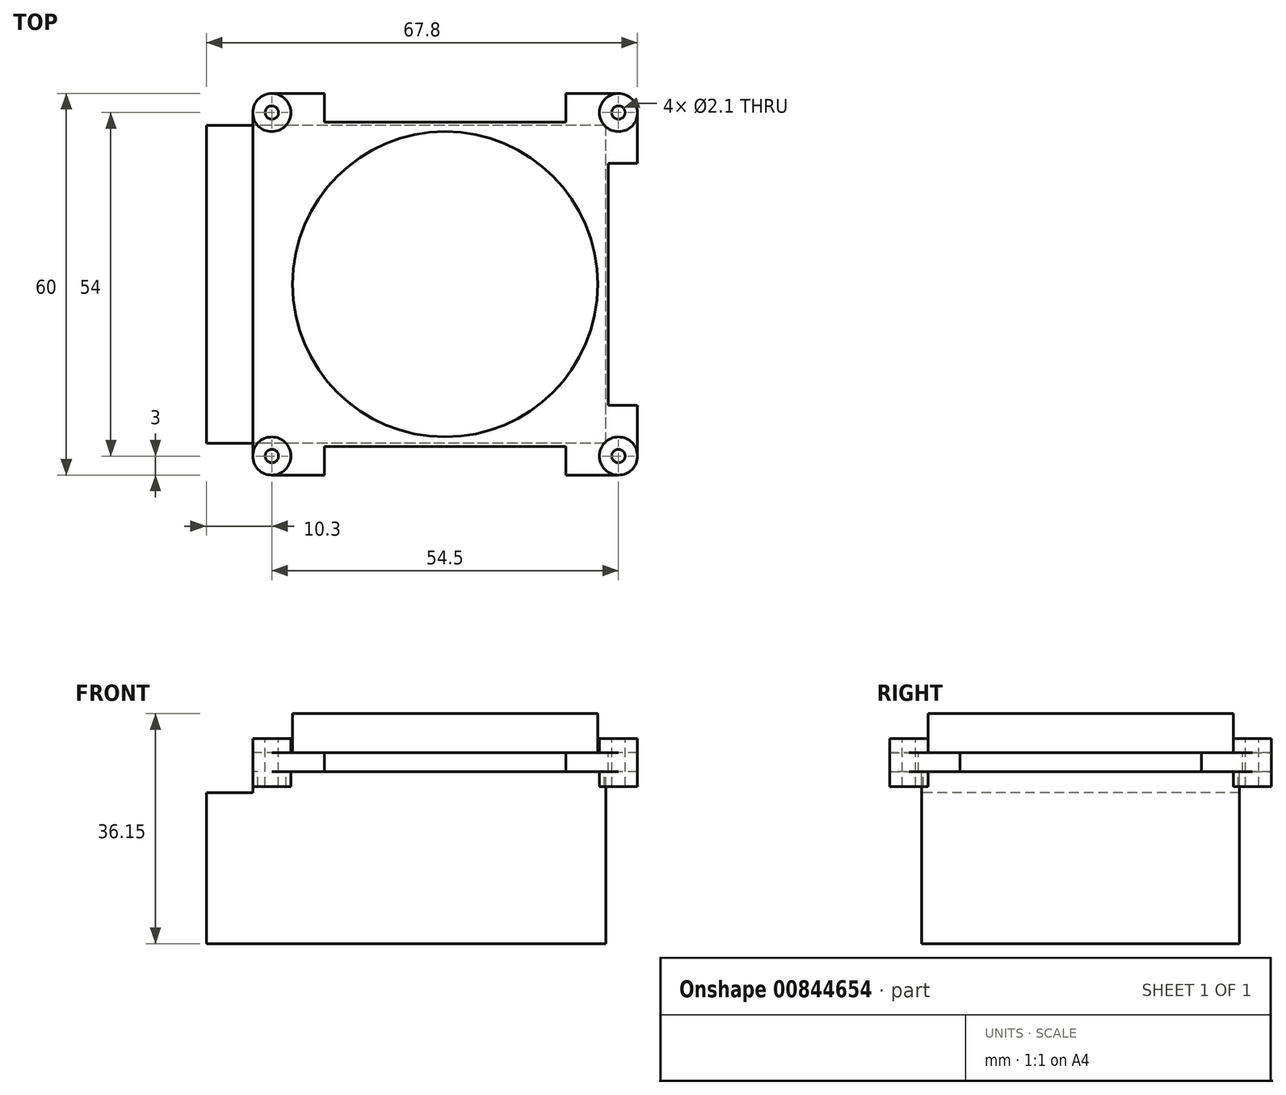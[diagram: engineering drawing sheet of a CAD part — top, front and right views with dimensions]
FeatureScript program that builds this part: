
annotation { "Feature Type Name" : "Feature", "Feature Type Description" : "" }
export const myFeature = defineFeature(function(context is Context, id is Id, definition is map)
    precondition{}
    {
        {
            var Q0;
            Q0=qCreatedBy(makeId("Top.planeOp"),FACE);
            var sketch = newSketch(context, id + "F0", { "sketchPlane" : qUnion([Q0])});
            skLineSegment(sketch, "E0.bottom", {"start": v(27.25, 30) * mm, "end": v(19, 30) * mm});
            skLineSegment(sketch, "E0.top", {"start": v(27.25, -30) * mm, "end": v(19, -30) * mm});
            skLineSegment(sketch, "E0.left", {"start": v(30.25, 27) * mm, "end": v(30.25, -27) * mm});
            skLineSegment(sketch, "E0.right", {"start": v(-30.25, 27) * mm, "end": v(-30.25, -27) * mm});
            skPoint(sketch, "E0.middle", {"position": v(0, 0) * mm});
            skCircle(sketch, "E1", {"center": v(0, 0) * mm, "radius": 24 * mm});
            skCircle(sketch, "E2", {"center": v(27.25, 27) * mm, "radius": 3 * mm});
            skCircle(sketch, "E3", {"center": v(-27.25, 27) * mm, "radius": 3 * mm});
            skCircle(sketch, "E4", {"center": v(-27.25, -27) * mm, "radius": 3 * mm});
            skCircle(sketch, "E5", {"center": v(27.25, -27) * mm, "radius": 3 * mm});
            skPoint(sketch, "E6.orphan", {"position": v(-30.25, 30) * mm});
            skPoint(sketch, "E7.orphan", {"position": v(30.25, 30) * mm});
            skPoint(sketch, "E8.orphan", {"position": v(30.25, -30) * mm});
            skPoint(sketch, "E9.orphan", {"position": v(-30.25, -30) * mm});
            skCircle(sketch, "E10", {"center": v(-27.25, 27) * mm, "radius": 1.05 * mm});
            skCircle(sketch, "E11", {"center": v(-27.25, -27) * mm, "radius": 1.05 * mm});
            skCircle(sketch, "E12", {"center": v(27.25, -27) * mm, "radius": 1.05 * mm});
            skCircle(sketch, "E13", {"center": v(27.25, 27) * mm, "radius": 1.05 * mm});
            skLineSegment(sketch, "E14.top", {"start": v(-19, 25.5) * mm, "end": v(19, 25.5) * mm});
            skLineSegment(sketch, "E14.left", {"start": v(-19, 30) * mm, "end": v(-19, 25.5) * mm});
            skLineSegment(sketch, "E14.right", {"start": v(19, 30) * mm, "end": v(19, 25.5) * mm});
            skLineSegment(sketch, "E15.trimOffspring", {"start": v(-19, 30) * mm, "end": v(-27.25, 30) * mm});
            skLineSegment(sketch, "E16.MirrorCS", {"start": v(-19, -30) * mm, "end": v(-19, -25.5) * mm});
            skLineSegment(sketch, "E17.MirrorCS", {"start": v(-19, -25.5) * mm, "end": v(19, -25.5) * mm});
            skLineSegment(sketch, "E18.MirrorCS", {"start": v(19, -30) * mm, "end": v(19, -25.5) * mm});
            skLineSegment(sketch, "E19.trimOffspring", {"start": v(-19, -30) * mm, "end": v(-27.25, -30) * mm});
            skLineSegment(sketch, "E20.bottom", {"start": v(30.25, -19) * mm, "end": v(25.65, -19) * mm});
            skLineSegment(sketch, "E20.top", {"start": v(30.25, 19) * mm, "end": v(25.65, 19) * mm});
            skLineSegment(sketch, "E20.left", {"start": v(30.25, -19) * mm, "end": v(30.25, 19) * mm});
            skLineSegment(sketch, "E20.right", {"start": v(25.65, -19) * mm, "end": v(25.65, 19) * mm});
            skSolve(sketch);
        }
        {
            var Q0;
            Q0=makeQuery(id+"F0.imprint","IMPRINT",FACE,{"disambiguationData":[TD([[makeQuery(id+"F0.imprint","IMPRINT",EDGE,{"derivedFrom":sQuery(id+"F0.wireOp",EDGE,"E1")}),1.0]])]});
            extrude(context, id + "F1", {"entities" : qUnion([Q0]), "depth" : 6.15 * mm, "offsetDistance" : 25 * mm});
        }
        {
            var Q0;
            Q0=makeQuery(id+"F0.imprint","IMPRINT",FACE,{"disambiguationData":[TD([[makeQuery(id+"F0.imprint","IMPRINT",EDGE,{"derivedFrom":sQuery(id+"F0.wireOp",EDGE,"E12")}),-1.0]])]});
            var Q1;
            Q1=makeQuery(id+"F0.imprint","IMPRINT",FACE,{"disambiguationData":[TD([[makeQuery(id+"F0.imprint","IMPRINT",EDGE,{"derivedFrom":sQuery(id+"F0.wireOp",EDGE,"E13")}),-1.0]])]});
            var Q2;
            Q2=makeQuery(id+"F0.imprint","IMPRINT",FACE,{"disambiguationData":[TD([[makeQuery(id+"F0.imprint","IMPRINT",EDGE,{"derivedFrom":sQuery(id+"F0.wireOp",EDGE,"E10")}),-1.0]])]});
            var Q3;
            Q3=makeQuery(id+"F0.imprint","IMPRINT",FACE,{"disambiguationData":[TD([[makeQuery(id+"F0.imprint","IMPRINT",EDGE,{"derivedFrom":sQuery(id+"F0.wireOp",EDGE,"E11")}),-1.0]])]});
            extrude(context, id + "F2", {"entities" : qUnion([Q0, Q1, Q2, Q3]), "depth" : 2.25 * mm, "offsetDistance" : 25 * mm});
        }
        {
            var Q0;
            Q0=makeQuery(id+"F0.imprint","IMPRINT",FACE,{"disambiguationData":[TD([[makeQuery(id+"F0.imprint","IMPRINT",EDGE,{"derivedFrom":sQuery(id+"F0.wireOp",EDGE,"E11")}),-1.0]])]});
            var Q1;
            Q1=makeQuery(id+"F0.imprint","IMPRINT",FACE,{"disambiguationData":[TD([[makeQuery(id+"F0.imprint","IMPRINT",EDGE,{"derivedFrom":sQuery(id+"F0.wireOp",EDGE,"E10")}),-1.0]])]});
            var Q2;
            Q2=makeQuery(id+"F0.imprint","IMPRINT",FACE,{"disambiguationData":[TD([[makeQuery(id+"F0.imprint","IMPRINT",EDGE,{"derivedFrom":sQuery(id+"F0.wireOp",EDGE,"E12")}),-1.0]])]});
            var Q3;
            Q3=makeQuery(id+"F0.imprint","IMPRINT",FACE,{"disambiguationData":[TD([[makeQuery(id+"F0.imprint","IMPRINT",EDGE,{"derivedFrom":sQuery(id+"F0.wireOp",EDGE,"E13")}),-1.0]])]});
            extrude(context, id + "F3", {"entities" : qUnion([Q0, Q1, Q2, Q3]), "oppositeDirection" : true, "depth" : 5.3 * mm, "offsetDistance" : 25 * mm});
        }
        {
            var Q0;
            {var subQ6=sQuery(id+"F0.wireOp",EDGE,"E0.bottom");Q0=makeQuery(id+"F0.imprint","IMPRINT",FACE,{"disambiguationData":[TD([[makeQuery(id+"F0.imprint","IMPRINT",EDGE,{"derivedFrom":subQ6}),1.0]])]});}
            extrude(context, id + "F4", {"entities" : qUnion([Q0]), "oppositeDirection" : true, "depth" : 3 * mm, "offsetDistance" : 25 * mm});
        }
        {
            var Q0;
            Q0=makeQuery(id+"F4.opExtrude","SWEPT_BODY",BODY,{"disambiguationData":[OSD([sQuery(id+"F0.wireOp",EDGE,"E0.bottom"),sQuery(id+"F0.wireOp",EDGE,"E0.top"),sQuery(id+"F0.wireOp",EDGE,"E0.left"),sQuery(id+"F0.wireOp",EDGE,"E0.right"),sQuery(id+"F0.wireOp",EDGE,"E1"),sQuery(id+"F0.wireOp",EDGE,"E2"),sQuery(id+"F0.wireOp",EDGE,"E3"),sQuery(id+"F0.wireOp",EDGE,"E4"),sQuery(id+"F0.wireOp",EDGE,"E5"),sQuery(id+"F0.wireOp",EDGE,"E14.top"),sQuery(id+"F0.wireOp",EDGE,"E14.left"),sQuery(id+"F0.wireOp",EDGE,"E14.right"),sQuery(id+"F0.wireOp",EDGE,"E15.trimOffspring"),sQuery(id+"F0.wireOp",EDGE,"E16.MirrorCS"),sQuery(id+"F0.wireOp",EDGE,"E17.MirrorCS"),sQuery(id+"F0.wireOp",EDGE,"E18.MirrorCS"),sQuery(id+"F0.wireOp",EDGE,"E19.trimOffspring")])]});
            var Q1;
            Q1=makeQuery(id+"F3.opExtrude","SWEPT_BODY",BODY,{"disambiguationData":[OSD([sQuery(id+"F0.wireOp",EDGE,"E5"),sQuery(id+"F0.wireOp",EDGE,"E12")])]});
            var Q2;
            Q2=makeQuery(id+"F3.opExtrude","SWEPT_BODY",BODY,{"disambiguationData":[OSD([sQuery(id+"F0.wireOp",EDGE,"E4"),sQuery(id+"F0.wireOp",EDGE,"E11")])]});
            var Q3;
            Q3=makeQuery(id+"F3.opExtrude","SWEPT_BODY",BODY,{"disambiguationData":[OSD([sQuery(id+"F0.wireOp",EDGE,"E3"),sQuery(id+"F0.wireOp",EDGE,"E10")])]});
            var Q4;
            Q4=makeQuery(id+"F3.opExtrude","SWEPT_BODY",BODY,{"disambiguationData":[OSD([sQuery(id+"F0.wireOp",EDGE,"E2"),sQuery(id+"F0.wireOp",EDGE,"E13")])]});
            var Q5;
            Q5=makeQuery(id+"F2.opExtrude","SWEPT_BODY",BODY,{"disambiguationData":[OSD([sQuery(id+"F0.wireOp",EDGE,"E5"),sQuery(id+"F0.wireOp",EDGE,"E12")])]});
            var Q6;
            Q6=makeQuery(id+"F2.opExtrude","SWEPT_BODY",BODY,{"disambiguationData":[OSD([sQuery(id+"F0.wireOp",EDGE,"E4"),sQuery(id+"F0.wireOp",EDGE,"E11")])]});
            var Q7;
            Q7=makeQuery(id+"F2.opExtrude","SWEPT_BODY",BODY,{"disambiguationData":[OSD([sQuery(id+"F0.wireOp",EDGE,"E3"),sQuery(id+"F0.wireOp",EDGE,"E10")])]});
            var Q8;
            Q8=makeQuery(id+"F2.opExtrude","SWEPT_BODY",BODY,{"disambiguationData":[OSD([sQuery(id+"F0.wireOp",EDGE,"E2"),sQuery(id+"F0.wireOp",EDGE,"E13")])]});
            var Q9;
            Q9=makeQuery(id+"F1.opExtrude","SWEPT_BODY",BODY,{"disambiguationData":[OSD([sQuery(id+"F0.wireOp",EDGE,"E1")])]});
            booleanBodies(context, id + "F5", {"operationType" : BooleanOperationType.UNION, "tools" : qUnion([Q0, Q1, Q2, Q3, Q4, Q5, Q6, Q7, Q8, Q9])});
        }
        {
            var Q0;
            Q0=makeQuery(id+"F0.imprint","IMPRINT",FACE,{"disambiguationData":[TD([[makeQuery(id+"F0.imprint","IMPRINT",EDGE,{"derivedFrom":sQuery(id+"F0.wireOp",EDGE,"E1")}),1.0]])]});
            var sketch = newSketch(context, id + "F6", { "sketchPlane" : qUnion([Q0])});
            skLineSegment(sketch, "E21.bottom", {"start": v(25.25, -25) * mm, "end": v(-30.25, -25) * mm});
            skLineSegment(sketch, "E21.top", {"start": v(25.25, 25) * mm, "end": v(-30.25, 25) * mm});
            skLineSegment(sketch, "E21.left", {"start": v(25.25, -25) * mm, "end": v(25.25, 25) * mm});
            skLineSegment(sketch, "E21.right", {"start": v(-30.25, -25) * mm, "end": v(-30.25, 25) * mm});
            skSolve(sketch);
        }
        {
            var Q0;
            Q0 = qSketchRegion(id + "F6", true);
            extrude(context, id + "F7", {"entities" : qUnion([Q0]), "oppositeDirection" : true, "depth" : 30 * mm, "offsetDistance" : 25 * mm});
        }
        {
            var Q0;
            Q0=makeQuery(id+"F4.opExtrude","SWEPT_BODY",BODY,{"disambiguationData":[OSD([sQuery(id+"F0.wireOp",EDGE,"E0.bottom"),sQuery(id+"F0.wireOp",EDGE,"E0.top"),sQuery(id+"F0.wireOp",EDGE,"E0.left"),sQuery(id+"F0.wireOp",EDGE,"E0.right"),sQuery(id+"F0.wireOp",EDGE,"E1"),sQuery(id+"F0.wireOp",EDGE,"E2"),sQuery(id+"F0.wireOp",EDGE,"E3"),sQuery(id+"F0.wireOp",EDGE,"E4"),sQuery(id+"F0.wireOp",EDGE,"E5"),sQuery(id+"F0.wireOp",EDGE,"E14.top"),sQuery(id+"F0.wireOp",EDGE,"E14.left"),sQuery(id+"F0.wireOp",EDGE,"E14.right"),sQuery(id+"F0.wireOp",EDGE,"E15.trimOffspring"),sQuery(id+"F0.wireOp",EDGE,"E16.MirrorCS"),sQuery(id+"F0.wireOp",EDGE,"E17.MirrorCS"),sQuery(id+"F0.wireOp",EDGE,"E18.MirrorCS"),sQuery(id+"F0.wireOp",EDGE,"E19.trimOffspring")])]});
            var Q1;
            {var subQ0=sQuery(id+"F0.wireOp",EDGE,"E5");var subQ1=sQuery(id+"F0.wireOp",EDGE,"E4");var subQ2=sQuery(id+"F0.wireOp",EDGE,"E3");var subQ3=sQuery(id+"F0.wireOp",EDGE,"E2");var subQ4=sQuery(id+"F0.wireOp",EDGE,"E1");var subQ5=sQuery(id+"F0.wireOp",EDGE,"E12");var subQ6=sQuery(id+"F0.wireOp",EDGE,"E11");var subQ7=sQuery(id+"F0.wireOp",EDGE,"E10");var subQ8=sQuery(id+"F0.wireOp",EDGE,"E13");Q1=makeQuery(id+"F5.opBoolean","MERGE",BODY,{"derivedFrom":[makeQuery(id+"F1.opExtrude","SWEPT_BODY",BODY,{"disambiguationData":[OSD([subQ4])]}),makeQuery(id+"F2.opExtrude","SWEPT_BODY",BODY,{"disambiguationData":[OSD([subQ3,subQ8])]}),makeQuery(id+"F2.opExtrude","SWEPT_BODY",BODY,{"disambiguationData":[OSD([subQ2,subQ7])]}),makeQuery(id+"F2.opExtrude","SWEPT_BODY",BODY,{"disambiguationData":[OSD([subQ1,subQ6])]}),makeQuery(id+"F2.opExtrude","SWEPT_BODY",BODY,{"disambiguationData":[OSD([subQ0,subQ5])]}),makeQuery(id+"F3.opExtrude","SWEPT_BODY",BODY,{"disambiguationData":[OSD([subQ3,subQ8])]}),makeQuery(id+"F3.opExtrude","SWEPT_BODY",BODY,{"disambiguationData":[OSD([subQ2,subQ7])]}),makeQuery(id+"F3.opExtrude","SWEPT_BODY",BODY,{"disambiguationData":[OSD([subQ1,subQ6])]}),makeQuery(id+"F3.opExtrude","SWEPT_BODY",BODY,{"disambiguationData":[OSD([subQ0,subQ5])]}),makeQuery(id+"F4.opExtrude","SWEPT_BODY",BODY,{"disambiguationData":[OSD([sQuery(id+"F0.wireOp",EDGE,"E0.bottom"),sQuery(id+"F0.wireOp",EDGE,"E0.top"),sQuery(id+"F0.wireOp",EDGE,"E0.left"),sQuery(id+"F0.wireOp",EDGE,"E0.right"),subQ4,subQ3,subQ2,subQ1,subQ0,sQuery(id+"F0.wireOp",EDGE,"E14.top"),sQuery(id+"F0.wireOp",EDGE,"E14.left"),sQuery(id+"F0.wireOp",EDGE,"E14.right"),sQuery(id+"F0.wireOp",EDGE,"E15.trimOffspring"),sQuery(id+"F0.wireOp",EDGE,"E16.MirrorCS"),sQuery(id+"F0.wireOp",EDGE,"E17.MirrorCS"),sQuery(id+"F0.wireOp",EDGE,"E18.MirrorCS"),sQuery(id+"F0.wireOp",EDGE,"E19.trimOffspring")])]})]});}
            var Q2;
            Q2=makeQuery(id+"F7.opExtrude","SWEPT_BODY",BODY,{"disambiguationData":[OSD([sQuery(id+"F6.wireOp",EDGE,"E21.bottom"),sQuery(id+"F6.wireOp",EDGE,"E21.top"),sQuery(id+"F6.wireOp",EDGE,"E21.left"),sQuery(id+"F6.wireOp",EDGE,"E21.right")])]});
            booleanBodies(context, id + "F8", {"operationType" : BooleanOperationType.UNION, "tools" : qUnion([Q0, Q1, Q2])});
        }
        {
            var Q0;
            Q0=makeQuery(id+"F8.opBoolean","MERGE",FACE,{"derivedFrom":[makeQuery(id+"F4.opExtrude","SWEPT_FACE",FACE,{"disambiguationData":[OSD([sQuery(id+"F0.wireOp",EDGE,"E0.right")])]}),makeQuery(id+"F7.opExtrude","SWEPT_FACE",FACE,{"disambiguationData":[OSD([sQuery(id+"F6.wireOp",EDGE,"E21.right")])]})]});
            var sketch = newSketch(context, id + "F9", { "sketchPlane" : qUnion([Q0])});
            skLineSegment(sketch, "E22.bottom", {"start": v(-25, -30) * mm, "end": v(25, -30) * mm});
            skLineSegment(sketch, "E22.top", {"start": v(-25, -6.3) * mm, "end": v(25, -6.3) * mm});
            skLineSegment(sketch, "E22.left", {"start": v(-25, -30) * mm, "end": v(-25, -6.3) * mm});
            skLineSegment(sketch, "E22.right", {"start": v(25, -30) * mm, "end": v(25, -6.3) * mm});
            skSolve(sketch);
        }
        {
            var Q0;
            Q0 = qSketchRegion(id + "F9", true);
            extrude(context, id + "F10", {"entities" : qUnion([Q0]), "operationType" : NewBodyOperationType.ADD, "depth" : 7.3 * mm, "offsetDistance" : 25 * mm});
        }
    });
